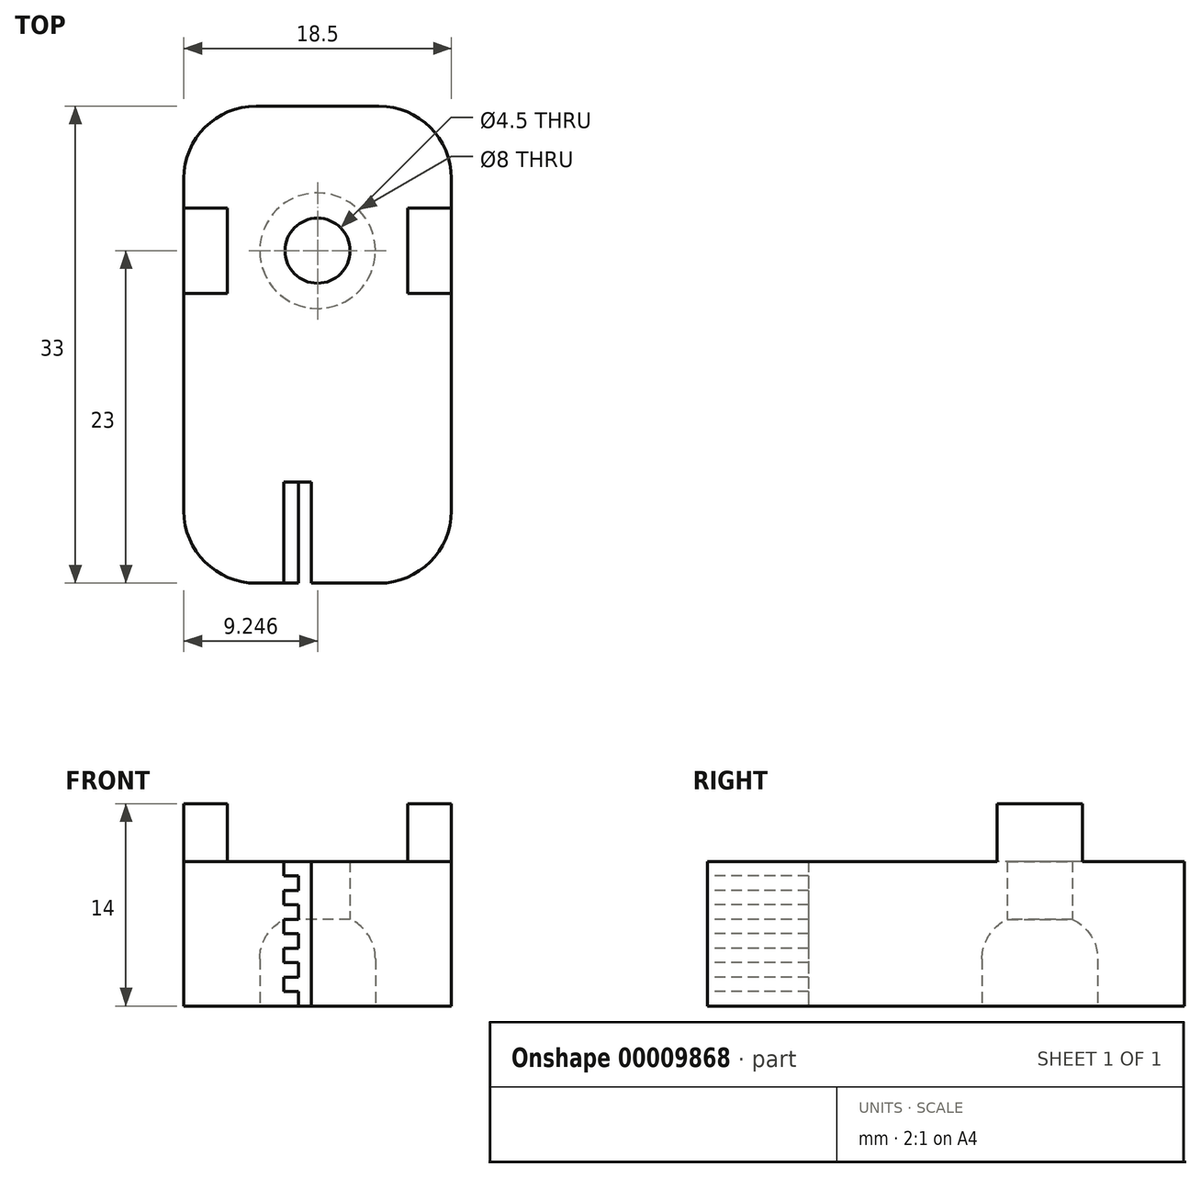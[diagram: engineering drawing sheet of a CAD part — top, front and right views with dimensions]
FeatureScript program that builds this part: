
annotation { "Feature Type Name" : "Feature", "Feature Type Description" : "" }
export const myFeature = defineFeature(function(context is Context, id is Id, definition is map)
    precondition{}
    {
        {
            var Q0;
            Q0=qCreatedBy(makeId("Top.planeOp"),FACE);
            var sketch = newSketch(context, id + "F0", { "sketchPlane" : qUnion([Q0])});
            skLineSegment(sketch, "E0.bottom", {"start": v(-4.96, 0) * mm, "end": v(13.54, 0) * mm});
            skLineSegment(sketch, "E0.top", {"start": v(-4.96, 33) * mm, "end": v(13.54, 33) * mm});
            skLineSegment(sketch, "E0.left", {"start": v(-4.96, 0) * mm, "end": v(-4.96, 33) * mm});
            skLineSegment(sketch, "E0.right", {"start": v(13.54, 0) * mm, "end": v(13.54, 33) * mm});
            skLineSegment(sketch, "E1", {"start": v(-4.96, 13) * mm, "end": v(13.54, 13) * mm});
            skLineSegment(sketch, "E2.bottom", {"start": v(-4.96, 25.95) * mm, "end": v(-1.96, 25.95) * mm});
            skLineSegment(sketch, "E2.top", {"start": v(-4.96, 20.05) * mm, "end": v(-1.96, 20.05) * mm});
            skLineSegment(sketch, "E2.left", {"start": v(-4.96, 25.95) * mm, "end": v(-4.96, 20.05) * mm});
            skLineSegment(sketch, "E2.right", {"start": v(-1.96, 25.95) * mm, "end": v(-1.96, 20.05) * mm});
            skLineSegment(sketch, "E3.bottom", {"start": v(13.54, 25.95) * mm, "end": v(10.54, 25.95) * mm});
            skLineSegment(sketch, "E3.top", {"start": v(13.54, 20.05) * mm, "end": v(10.54, 20.05) * mm});
            skLineSegment(sketch, "E3.left", {"start": v(13.54, 25.95) * mm, "end": v(13.54, 20.05) * mm});
            skLineSegment(sketch, "E3.right", {"start": v(10.54, 25.95) * mm, "end": v(10.54, 20.05) * mm});
            skCircle(sketch, "E4", {"center": v(4.29, 23) * mm, "radius": 2.25 * mm});
            skPoint(sketch, "E5", {"position": v(-1.96, 23) * mm});
            skPoint(sketch, "E6", {"position": v(-4.96, 23) * mm});
            skLineSegment(sketch, "E7", {"start": v(-4.96, 23) * mm, "end": v(13.54, 23) * mm});
            skSolve(sketch);
        }
        {
            var Q0;
            {var subQ2=sQuery(id+"F0.wireOp",EDGE,"E0.top");Q0=makeQuery(id+"F0.imprint","IMPRINT",FACE,{"disambiguationData":[TD([[makeQuery(id+"F0.imprint","IMPRINT",EDGE,{"derivedFrom":subQ2}),-1.0]])]});}
            var Q1;
            {var subQ1=sQuery(id+"F0.wireOp",EDGE,"E1");Q1=makeQuery(id+"F0.imprint","IMPRINT",FACE,{"disambiguationData":[TD([[makeQuery(id+"F0.imprint","IMPRINT",EDGE,{"derivedFrom":subQ1}),1.0]])]});}
            var Q2;
            {var subQ0=sQuery(id+"F0.wireOp",EDGE,"E0.bottom");Q2=makeQuery(id+"F0.imprint","IMPRINT",FACE,{"disambiguationData":[TD([[makeQuery(id+"F0.imprint","IMPRINT",EDGE,{"derivedFrom":subQ0}),1.0]])]});}
            extrude(context, id + "F1", {"entities" : qUnion([Q0, Q1, Q2]), "depth" : 10 * mm});
        }
        {
            var Q0;
            {var subQ0=sQuery(id+"F0.wireOp",EDGE,"E2.top");Q0=makeQuery(id+"F0.imprint","IMPRINT",FACE,{"disambiguationData":[TD([[makeQuery(id+"F0.imprint","IMPRINT",EDGE,{"derivedFrom":subQ0}),1.0]])]});}
            var Q1;
            {var subQ0=sQuery(id+"F0.wireOp",EDGE,"E2.bottom");Q1=makeQuery(id+"F0.imprint","IMPRINT",FACE,{"disambiguationData":[TD([[makeQuery(id+"F0.imprint","IMPRINT",EDGE,{"derivedFrom":subQ0}),-1.0]])]});}
            var Q2;
            {var subQ0=sQuery(id+"F0.wireOp",EDGE,"E3.bottom");Q2=makeQuery(id+"F0.imprint","IMPRINT",FACE,{"disambiguationData":[TD([[makeQuery(id+"F0.imprint","IMPRINT",EDGE,{"derivedFrom":subQ0}),1.0]])]});}
            var Q3;
            {var subQ0=sQuery(id+"F0.wireOp",EDGE,"E3.top");Q3=makeQuery(id+"F0.imprint","IMPRINT",FACE,{"disambiguationData":[TD([[makeQuery(id+"F0.imprint","IMPRINT",EDGE,{"derivedFrom":subQ0}),-1.0]])]});}
            extrude(context, id + "F2", {"entities" : qUnion([Q0, Q1, Q2, Q3]), "operationType" : NewBodyOperationType.ADD, "depth" : 14 * mm});
        }
        {
            var Q0;
            Q0=makeQuery(id+"F1.opExtrude","SWEPT_FACE",FACE,{"disambiguationData":[OSD([sQuery(id+"F0.wireOp",EDGE,"E0.bottom")])]});
            var sketch = newSketch(context, id + "F3", { "sketchPlane" : qUnion([Q0])});
            skLineSegment(sketch, "E8", {"start": v(1.96, 10) * mm, "end": v(1.96, 9) * mm});
            skLineSegment(sketch, "E9", {"start": v(1.96, 9) * mm, "end": v(2.96, 9) * mm});
            skLineSegment(sketch, "E10", {"start": v(2.96, 9) * mm, "end": v(2.96, 8) * mm});
            skLineSegment(sketch, "E11", {"start": v(2.96, 8) * mm, "end": v(1.96, 8) * mm});
            skLineSegment(sketch, "E12", {"start": v(1.96, 8) * mm, "end": v(1.96, 7) * mm});
            skLineSegment(sketch, "E13", {"start": v(1.96, 7) * mm, "end": v(2.96, 7) * mm});
            skLineSegment(sketch, "E14", {"start": v(2.96, 7) * mm, "end": v(2.96, 6) * mm});
            skLineSegment(sketch, "E15", {"start": v(2.96, 6) * mm, "end": v(1.96, 6) * mm});
            skLineSegment(sketch, "E16", {"start": v(1.96, 6) * mm, "end": v(1.96, 5) * mm});
            skLineSegment(sketch, "E17", {"start": v(1.96, 5) * mm, "end": v(2.96, 5) * mm});
            skLineSegment(sketch, "E18", {"start": v(2.96, 5) * mm, "end": v(2.96, 4) * mm});
            skLineSegment(sketch, "E19", {"start": v(2.96, 4) * mm, "end": v(1.96, 4) * mm});
            skLineSegment(sketch, "E20", {"start": v(1.96, 4) * mm, "end": v(1.96, 3) * mm});
            skLineSegment(sketch, "E21", {"start": v(1.96, 3) * mm, "end": v(2.96, 3) * mm});
            skLineSegment(sketch, "E22", {"start": v(2.96, 3) * mm, "end": v(2.96, 2) * mm});
            skLineSegment(sketch, "E23", {"start": v(2.96, 2) * mm, "end": v(1.96, 2) * mm});
            skLineSegment(sketch, "E24", {"start": v(1.96, 2) * mm, "end": v(1.96, 1) * mm});
            skLineSegment(sketch, "E25", {"start": v(1.96, 1) * mm, "end": v(2.96, 1) * mm});
            skLineSegment(sketch, "E26", {"start": v(2.96, 1) * mm, "end": v(2.96, 0) * mm});
            skLineSegment(sketch, "E27", {"start": v(2.96, 0) * mm, "end": v(1.96, 0) * mm});
            skLineSegment(sketch, "E28", {"start": v(3.86, 10) * mm, "end": v(3.86, 0) * mm});
            skLineSegment(sketch, "E29", {"start": v(1.96, 10) * mm, "end": v(3.86, 10) * mm});
            skLineSegment(sketch, "E30", {"start": v(3.86, 0) * mm, "end": v(2.96, 0) * mm});
            skSolve(sketch);
        }
        {
            var Q0;
            Q0=makeQuery(id+"F3.imprint","IMPRINT",FACE,{"disambiguationData":[TD([[makeQuery(id+"F3.imprint","IMPRINT",EDGE,{"derivedFrom":sQuery(id+"F3.wireOp",EDGE,"E8")}),1.0]])]});
            extrude(context, id + "F4", {"entities" : qUnion([Q0]), "operationType" : NewBodyOperationType.REMOVE, "oppositeDirection" : true, "depth" : 7 * mm});
        }
        {
            var Q0;
            {var subQ0=sQuery(id+"F0.wireOp",EDGE,"E3.right");var subQ1=sQuery(id+"F0.wireOp",EDGE,"E3.top");var subQ2=sQuery(id+"F0.wireOp",EDGE,"E3.bottom");var subQ3=sQuery(id+"F0.wireOp",EDGE,"E2.right");var subQ4=sQuery(id+"F0.wireOp",EDGE,"E2.top");var subQ5=sQuery(id+"F0.wireOp",EDGE,"E2.bottom");Q0=makeQuery(id+"F2.boolean.opBoolean","MERGE",FACE,{"derivedFrom":[makeQuery(id+"F1.opExtrude","CAP_FACE",FACE,{"disambiguationData":[OSD([sQuery(id+"F0.wireOp",EDGE,"E0.bottom"),sQuery(id+"F0.wireOp",EDGE,"E0.top"),sQuery(id+"F0.wireOp",EDGE,"E0.left"),sQuery(id+"F0.wireOp",EDGE,"E0.right"),subQ5,subQ4,subQ3,subQ2,subQ1,subQ0,sQuery(id+"F0.wireOp",EDGE,"E4")])],"isStart":true}),makeQuery(id+"F2.opExtrude","CAP_FACE",FACE,{"disambiguationData":[OSD([subQ5,subQ4,sQuery(id+"F0.wireOp",EDGE,"E2.left"),subQ3])],"isStart":true}),makeQuery(id+"F2.opExtrude","CAP_FACE",FACE,{"disambiguationData":[OSD([subQ2,subQ1,sQuery(id+"F0.wireOp",EDGE,"E3.left"),subQ0])],"isStart":true})]});}
            var sketch = newSketch(context, id + "F5", { "sketchPlane" : qUnion([Q0])});
            skCircle(sketch, "E31", {"center": v(4.29, -23) * mm, "radius": 4 * mm});
            skSolve(sketch);
        }
        {
            var Q0;
            Q0=makeQuery(id+"F5.imprint","IMPRINT",FACE,{"disambiguationData":[TD([[makeQuery(id+"F5.imprint","IMPRINT",EDGE,{"derivedFrom":sQuery(id+"F5.wireOp",EDGE,"E31")}),1.0]])]});
            extrude(context, id + "F6", {"entities" : qUnion([Q0]), "operationType" : NewBodyOperationType.REMOVE, "oppositeDirection" : true, "depth" : 6 * mm});
        }
        {
            var Q0;
            Q0=makeQuery(id+"F6.boolean.opBoolean","COPY",EDGE,{"derivedFrom":makeQuery(id+"F6.opExtrude","CAP_EDGE",EDGE,{"disambiguationData":[OSD([sQuery(id+"F5.wireOp",EDGE,"E31")])],"isStart":false})});
            fillet(context, id + "F7", {"entities" : qUnion([Q0]), "radius" : 3 * mm, "tangentPropagation" : true, "allowEdgeOverflow" : false});
        }
        {
            var Q0;
            Q0=makeQuery(id+"F1.opExtrude","SWEPT_EDGE",EDGE,{"disambiguationData":[OSD([sQuery(id+"F0.wireOp",EDGE,"E0.top"),sQuery(id+"F0.wireOp",EDGE,"E0.right")])]});
            var Q1;
            Q1=makeQuery(id+"F1.opExtrude","SWEPT_EDGE",EDGE,{"disambiguationData":[OSD([sQuery(id+"F0.wireOp",EDGE,"E0.top"),sQuery(id+"F0.wireOp",EDGE,"E0.left")])]});
            var Q2;
            Q2=makeQuery(id+"F1.opExtrude","SWEPT_EDGE",EDGE,{"disambiguationData":[OSD([sQuery(id+"F0.wireOp",EDGE,"E0.bottom"),sQuery(id+"F0.wireOp",EDGE,"E0.left")])]});
            var Q3;
            Q3=makeQuery(id+"F1.opExtrude","SWEPT_EDGE",EDGE,{"disambiguationData":[OSD([sQuery(id+"F0.wireOp",EDGE,"E0.bottom"),sQuery(id+"F0.wireOp",EDGE,"E0.right")])]});
            fillet(context, id + "F8", {"entities" : qUnion([Q0, Q1, Q2, Q3]), "radius" : 5 * mm, "tangentPropagation" : true, "allowEdgeOverflow" : false});
        }
    });
